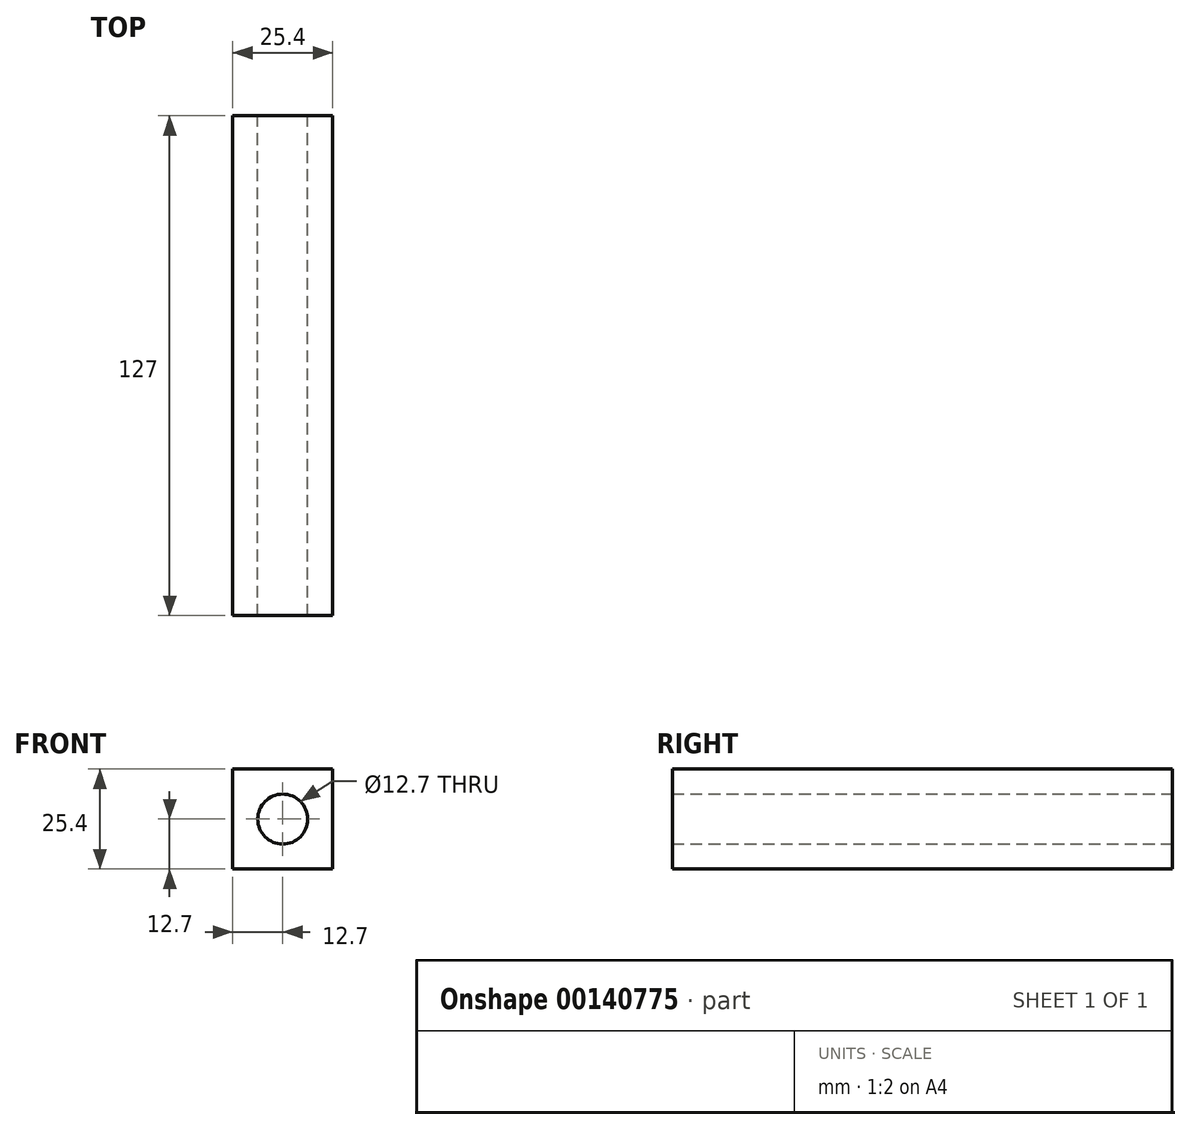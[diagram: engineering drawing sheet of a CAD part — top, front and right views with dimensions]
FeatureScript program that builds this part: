
annotation { "Feature Type Name" : "Feature", "Feature Type Description" : "" }
export const myFeature = defineFeature(function(context is Context, id is Id, definition is map)
    precondition{}
    {
        {
            var Q0;
            Q0=qCreatedBy(makeId("Front.planeOp"),FACE);
            var sketch = newSketch(context, id + "F0", { "sketchPlane" : qUnion([Q0])});
            skLineSegment(sketch, "E0.bottom", {"start": v(12.7, 12.7) * mm, "end": v(-12.7, 12.7) * mm});
            skLineSegment(sketch, "E0.top", {"start": v(12.7, -12.7) * mm, "end": v(-12.7, -12.7) * mm});
            skLineSegment(sketch, "E0.left", {"start": v(12.7, 12.7) * mm, "end": v(12.7, -12.7) * mm});
            skLineSegment(sketch, "E0.right", {"start": v(-12.7, 12.7) * mm, "end": v(-12.7, -12.7) * mm});
            skPoint(sketch, "E0.middle", {"position": v(0, 0) * mm});
            skSolve(sketch);
        }
        {
            var Q0;
            Q0 = qSketchRegion(id + "F0", true);
            extrude(context, id + "F1", {"entities" : qUnion([Q0]), "depth" : 127 * mm});
        }
        {
            var Q0;
            Q0=makeQuery(id+"F1.opExtrude","CAP_FACE",FACE,{"disambiguationData":[OSD([sQuery(id+"F0.wireOp",EDGE,"E0.bottom"),sQuery(id+"F0.wireOp",EDGE,"E0.top"),sQuery(id+"F0.wireOp",EDGE,"E0.left"),sQuery(id+"F0.wireOp",EDGE,"E0.right")])],"isStart":true});
            var sketch = newSketch(context, id + "F2", { "sketchPlane" : qUnion([Q0])});
            skCircle(sketch, "E1", {"center": v(0, 0) * mm, "radius": 6.35 * mm});
            skSolve(sketch);
        }
        {
            var Q0;
            Q0 = qSketchRegion(id + "F2", true);
            var Q1;
            Q1=makeQuery(id+"F1.opExtrude","CAP_FACE",FACE,{"disambiguationData":[OSD([sQuery(id+"F0.wireOp",EDGE,"E0.bottom"),sQuery(id+"F0.wireOp",EDGE,"E0.top"),sQuery(id+"F0.wireOp",EDGE,"E0.left"),sQuery(id+"F0.wireOp",EDGE,"E0.right")])],"isStart":false});
            extrude(context, id + "F3", {"entities" : qUnion([Q0]), "operationType" : NewBodyOperationType.REMOVE, "endBound" : BoundingType.UP_TO_SURFACE, "oppositeDirection" : true, "endBoundEntityFace" : qUnion([Q1]), "depth" : 25.4 * mm});
        }
    });
